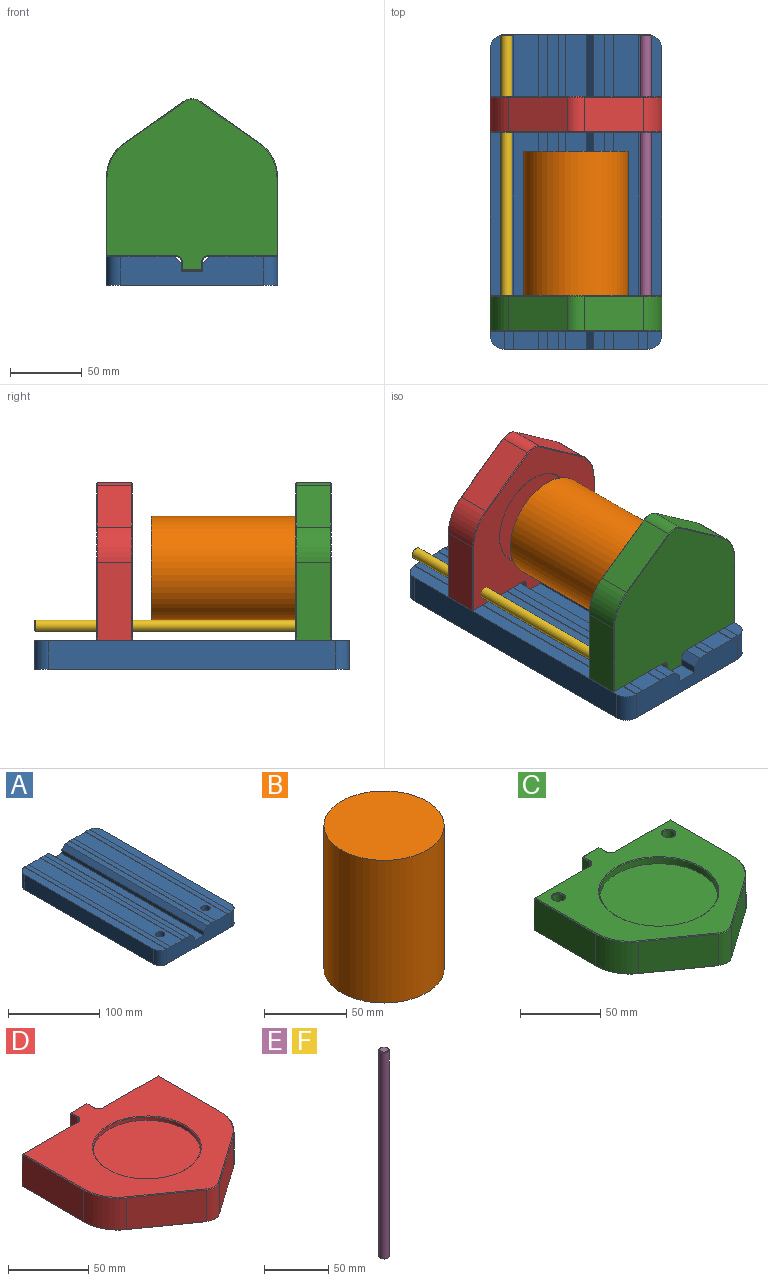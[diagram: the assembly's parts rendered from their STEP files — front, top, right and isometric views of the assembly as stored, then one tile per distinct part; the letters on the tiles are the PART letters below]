
ASSEMBLY  parts=6 mates=10
PART A: 34 faces, bbox 120x220x20.5 mm
  f0: plane 220x18mm, normal (0,0,1), area 3878.3mm2, adj f7,f11,f21,f29,f31
  f1: plane 220x7.45mm, normal (0,0,1), area 1639mm2, adj f7,f11,f18,f28
  f2: plane 220x10mm, normal (0,0,1), area 2157.1mm2, adj f6,f12,f13,f25
  f3: plane 220x18mm, normal (0,0,1), area 3878.3mm2, adj f7,f11,f20,f22,f26
  f4: plane 220x120mm, normal (0,0,-1), area 26150.7mm2, adj f6,f7,f8,f9,f10,f11,f12,f13
  f5: plane 220x10mm, normal (0,0,1), area 2157.1mm2, adj f8,f9,f10,f32
  f6: cylinder r=10mm len=20mm, axis (0,0,-1), area 314.2mm2, adj f2,f4,f7,f13
  f7: plane 100x20.5mm, normal (0,-1,0), area 1833mm2, adj f0,f1,f3,f4,f6,f8,f14,f15
  f8: cylinder r=10mm len=20mm, axis (0,0,-1), area 314.2mm2, adj f4,f5,f7,f9
  f9: plane 200x20mm, normal (1,0,0), area 4000mm2, adj f4,f5,f8,f10
  f10: cylinder r=10mm len=20mm, axis (0,0,-1), area 314.2mm2, adj f4,f5,f9,f11
  f11: plane 100x20.5mm, normal (0,1,0), area 1833mm2, adj f0,f1,f3,f4,f10,f12,f14,f15
  f12: cylinder r=10mm len=20mm, axis (0,0,-1), area 314.2mm2, adj f2,f4,f11,f13
  f13: plane 200x20mm, normal (-1,0,0), area 4000mm2, adj f2,f4,f6,f12
  f14: plane 220x7.45mm, normal (0,0,1), area 1639mm2, adj f7,f11,f19,f23
  f15: plane 220x5.2mm, normal (1,0,0), area 1144mm2, adj f7,f11,f17,f19
  f16: plane 220x5.2mm, normal (-1,0,0), area 1144mm2, adj f7,f11,f17,f18
  f17: plane 220x15.1mm, normal (0,0,1), area 3322mm2, adj f7,f11,f15,f16
  f18: plane 220x5mm, normal (-0.71,0,0.71), area 1555.6mm2, adj f1,f7,f11,f16
  f19: plane 220x5mm, normal (0.71,0,0.71), area 1555.6mm2, adj f7,f11,f14,f15
  f20: cylinder r=5.1mm len=20mm, axis (0,0,1), area 640.9mm2, adj f3,f4
  f21: cylinder r=5.1mm len=20mm, axis (0,0,1), area 640.9mm2, adj f0,f4
  f22: plane 220x0.5mm, normal (-1,0,0), area 110mm2, adj f3,f7,f11,f24
  f23: plane 220x0.5mm, normal (1,0,0), area 110mm2, adj f7,f11,f14,f24
  f24: plane 220x6mm, normal (0,0,1), area 1320mm2, adj f7,f11,f22,f23
  f25: plane 220x0.5mm, normal (-1,0,0), area 110mm2, adj f2,f7,f11,f27
  f26: plane 220x0.5mm, normal (1,0,0), area 110mm2, adj f3,f7,f11,f27
  f27: plane 220x6mm, normal (0,0,1), area 1320mm2, adj f7,f11,f25,f26
  f28: plane 220x0.5mm, normal (-1,0,0), area 110mm2, adj f1,f7,f11,f30
  f29: plane 220x0.5mm, normal (1,0,0), area 110mm2, adj f0,f7,f11,f30
  f30: plane 220x6mm, normal (0,0,1), area 1320mm2, adj f7,f11,f28,f29
  f31: plane 220x0.5mm, normal (-1,0,0), area 110mm2, adj f0,f7,f11,f33
  f32: plane 220x0.5mm, normal (1,0,0), area 110mm2, adj f5,f7,f11,f33
  f33: plane 220x6mm, normal (0,0,1), area 1320mm2, adj f7,f11,f31,f32
PART B: 3 faces, bbox 73x73x106 mm
  f0: cylinder r=36.5mm len=106mm, axis (0,0,-1), area 24309.6mm2, adj f1,f2
  f1: plane 73x73mm, normal (0,0,1), area 4185.4mm2, adj f0
  f2: plane 73x73mm, normal (0,0,-1), area 4185.4mm2, adj f0
PART C: 65 faces, bbox 120x120.2x25 mm
  f0: plane 119.2x119mm, normal (0,0,1), area 6258.4mm2, adj f26,f27,f28,f29,f30,f31,f32,f33
  f1: plane 24x13.9mm, normal (0,1,0), area 333.6mm2, adj f41,f42,f48,f49
  f2: plane 24x5.7mm, normal (-1,0,0), area 136.8mm2, adj f3,f43,f49,f53
  f3: cylinder r=4mm len=24mm, axis (0,0,1), area 150.8mm2, adj f2,f4,f38,f55
  f4: plane 48.55x24mm, normal (0,1,0), area 1070.2mm2, adj f3,f5,f36,f57,f60
  f5: plane 54.43x24mm, normal (-1,0,0), area 1306.3mm2, adj f4,f14,f34,f59
  f6: plane 41.51x29.22mm, normal (-0.58,-0.82,0), area 1218.3mm2, adj f7,f14,f30,f56
  f7: cylinder r=10mm len=24mm, axis (0,0,1), area 294.4mm2, adj f6,f8,f28,f54
  f8: plane 41.51x29.22mm, normal (0.58,-0.82,0), area 1218.3mm2, adj f7,f15,f26,f52
  f9: plane 54.43x24mm, normal (1,0,0), area 1306.3mm2, adj f10,f15,f29,f47
  f10: plane 48.55x24mm, normal (0,1,0), area 1070.2mm2, adj f9,f11,f31,f44,f61
  f11: cylinder r=4mm len=24mm, axis (0,0,1), area 150.8mm2, adj f10,f12,f33,f39
  f12: plane 24x5.7mm, normal (1,0,0), area 136.8mm2, adj f11,f35,f40,f41
  f13: plane 119.2x119mm, normal (0,0,-1), area 10803.5mm2, adj f39,f40,f44,f47,f48,f50,f52,f53
  f14: cylinder r=30mm len=24.53mm, axis (0,0,1), area 689.4mm2, adj f5,f6,f32,f58
  f15: cylinder r=30mm len=24.53mm, axis (0,0,1), area 689.4mm2, adj f8,f9,f27,f50
  f16: cylinder r=37mm len=74mm, axis (0,0,1), area 1046.2mm2, adj f17,f63
  f17: plane 74x74mm, normal (0,0,1), area 4300.8mm2, adj f16
  f18: cylinder r=4mm len=14.5mm, axis (0,0,1), area 364.4mm2, adj f19,f64
  f19: plane 8x8mm, normal (0,0,1), area 50.3mm2, adj f18
  f20: cylinder r=4mm len=14.5mm, axis (0,0,1), area 364.4mm2, adj f21,f62
  f21: plane 8x8mm, normal (0,0,1), area 50.3mm2, adj f20
  f22: cylinder r=5mm len=14.5mm, axis (0,1,0), area 455.5mm2, adj f23,f61
  f23: plane 10x10mm, normal (0,1,0), area 78.5mm2, adj f22
  f24: cylinder r=5mm len=14.5mm, axis (0,1,0), area 455.5mm2, adj f25,f60
  f25: plane 10x10mm, normal (0,1,0), area 78.5mm2, adj f24
  f26: plane 41.8x29.62mm, normal (0.41,-0.58,0.71), area 35.9mm2, adj f0,f8,f27,f28
  f27: cone r=29.5mm half-angle=45deg, axis (0,0,-1), area 20.1mm2, adj f0,f15,f26,f29
  f28: cone r=9.5mm half-angle=45deg, axis (0,0,-1), area 8.5mm2, adj f0,f7,f26,f30
  f29: plane 54.43x0.5mm, normal (0.71,0,0.71), area 38.3mm2, adj f0,f9,f27,f31
  f30: plane 41.8x29.62mm, normal (-0.41,-0.58,0.71), area 35.9mm2, adj f0,f6,f28,f32
  f31: plane 48.55x0.5mm, normal (0,0.71,0.71), area 34.2mm2, adj f0,f10,f29,f33
  f32: cone r=29.5mm half-angle=45deg, axis (0,0,-1), area 20.1mm2, adj f0,f14,f30,f34
  f33: cone r=4mm half-angle=45deg, axis (0,0,1), area 4.7mm2, adj f0,f11,f31,f35
  f34: plane 54.43x0.5mm, normal (-0.71,0,0.71), area 38.3mm2, adj f0,f5,f32,f36
  f35: plane 5.7x0.5mm, normal (0.71,0,0.71), area 4mm2, adj f0,f12,f33,f37
  f36: plane 48.55x0.5mm, normal (0,0.71,0.71), area 34.2mm2, adj f0,f4,f34,f38
  f37: plane 0.5x0.5mm, normal (0.58,0.58,0.58), area 0.2mm2, adj f35,f41,f42
  f38: cone r=4mm half-angle=45deg, axis (0,0,1), area 4.7mm2, adj f0,f3,f36,f43
  f39: cone r=4.5mm half-angle=45deg, axis (0,0,-1), area 4.7mm2, adj f11,f13,f40,f44
  f40: plane 5.7x0.5mm, normal (0.71,0,-0.71), area 4mm2, adj f12,f13,f39,f45
  f41: plane 24x0.5mm, normal (0.71,0.71,0), area 17mm2, adj f1,f12,f37,f45
  f42: plane 13.9x0.5mm, normal (0,0.71,0.71), area 9.8mm2, adj f0,f1,f37,f46
  f43: plane 5.7x0.5mm, normal (-0.71,0,0.71), area 4mm2, adj f0,f2,f38,f46
  f44: plane 48.55x0.5mm, normal (0,0.71,-0.71), area 34.2mm2, adj f10,f13,f39,f47
  f45: plane 0.5x0.5mm, normal (0.58,0.58,-0.58), area 0.2mm2, adj f40,f41,f48
  f46: plane 0.5x0.5mm, normal (-0.58,0.58,0.58), area 0.2mm2, adj f42,f43,f49
  f47: plane 54.43x0.5mm, normal (0.71,0,-0.71), area 38.3mm2, adj f9,f13,f44,f50
  f48: plane 13.9x0.5mm, normal (0,0.71,-0.71), area 9.8mm2, adj f1,f13,f45,f51
  f49: plane 24x0.5mm, normal (-0.71,0.71,0), area 17mm2, adj f1,f2,f46,f51
  f50: cone r=29.5mm half-angle=45deg, axis (0,0,1), area 20.1mm2, adj f13,f15,f47,f52
  f51: plane 0.5x0.5mm, normal (-0.58,0.58,-0.58), area 0.2mm2, adj f48,f49,f53
  f52: plane 41.8x29.62mm, normal (0.41,-0.58,-0.71), area 35.9mm2, adj f8,f13,f50,f54
  f53: plane 5.7x0.5mm, normal (-0.71,0,-0.71), area 4mm2, adj f2,f13,f51,f55
  f54: cone r=10mm half-angle=45deg, axis (0,0,1), area 8.5mm2, adj f7,f13,f52,f56
  f55: cone r=4.5mm half-angle=45deg, axis (0,0,-1), area 4.7mm2, adj f3,f13,f53,f57
  f56: plane 41.8x29.62mm, normal (-0.41,-0.58,-0.71), area 35.9mm2, adj f6,f13,f54,f58
  f57: plane 48.55x0.5mm, normal (0,0.71,-0.71), area 34.2mm2, adj f4,f13,f55,f59
  f58: cone r=29.5mm half-angle=45deg, axis (0,0,1), area 20.1mm2, adj f13,f14,f56,f59
  f59: plane 54.43x0.5mm, normal (-0.71,0,-0.71), area 38.3mm2, adj f5,f13,f57,f58
  f60: cone r=5.5mm half-angle=45deg, axis (0,1,0), area 23.3mm2, adj f4,f24
  f61: cone r=5mm half-angle=45deg, axis (0,1,0), area 23.3mm2, adj f10,f22
  f62: cone r=4.5mm half-angle=45deg, axis (0,0,1), area 18.9mm2, adj f0,f20
  f63: cone r=37mm half-angle=45deg, axis (0,0,1), area 165.5mm2, adj f0,f16
  f64: cone r=4mm half-angle=45deg, axis (0,0,1), area 18.9mm2, adj f0,f18
PART D: 47 faces, bbox 120x120.2x25 mm
  f0: plane 24x14.9mm, normal (0,1,0), area 357.6mm2, adj f1,f11,f23,f37
  f1: plane 24x6.2mm, normal (-1,0,0), area 148.8mm2, adj f0,f2,f21,f39
  f2: cylinder r=4mm len=24mm, axis (0,0,1), area 150.8mm2, adj f1,f3,f19,f41
  f3: plane 48.55x24mm, normal (0,1,0), area 1165.2mm2, adj f2,f4,f18,f43
  f4: plane 54.43x24mm, normal (-1,0,0), area 1306.3mm2, adj f3,f14,f20,f45
  f5: plane 41.51x29.22mm, normal (-0.58,-0.82,0), area 1218.3mm2, adj f6,f14,f24,f42
  f6: cylinder r=10mm len=24mm, axis (0,0,1), area 294.4mm2, adj f5,f7,f26,f40
  f7: plane 41.51x29.22mm, normal (0.58,-0.82,0), area 1218.3mm2, adj f6,f15,f28,f38
  f8: plane 54.43x24mm, normal (1,0,0), area 1306.3mm2, adj f9,f15,f31,f34
  f9: plane 48.55x24mm, normal (0,1,0), area 1165.2mm2, adj f8,f10,f29,f32
  f10: cylinder r=4mm len=24mm, axis (0,0,1), area 150.8mm2, adj f9,f11,f27,f33
  f11: plane 24x6.2mm, normal (1,0,0), area 148.8mm2, adj f0,f10,f25,f35
  f12: plane 119.2x119mm, normal (0,0,-1), area 10803.5mm2, adj f32,f33,f34,f35,f36,f37,f38,f39
  f13: plane 119.2x119mm, normal (0,0,1), area 7183.5mm2, adj f18,f19,f20,f21,f22,f23,f24,f25
  f14: cylinder r=30mm len=24.53mm, axis (0,0,1), area 689.4mm2, adj f4,f5,f22,f44
  f15: cylinder r=30mm len=24.53mm, axis (0,0,1), area 689.4mm2, adj f7,f8,f30,f36
  f16: cylinder r=33.45mm len=66.89mm, axis (0,0,1), area 525.4mm2, adj f17,f46
  f17: plane 66.89x66.89mm, normal (0,0,1), area 3514.1mm2, adj f16
  f18: plane 48.55x0.5mm, normal (0,0.71,0.71), area 34.2mm2, adj f3,f13,f19,f20
  f19: cone r=4mm half-angle=45deg, axis (0,0,1), area 4.7mm2, adj f2,f13,f18,f21
  f20: plane 54.43x0.5mm, normal (-0.71,0,0.71), area 38.3mm2, adj f4,f13,f18,f22
  f21: plane 6.2x0.5mm, normal (-0.71,0,0.71), area 4.2mm2, adj f1,f13,f19,f23
  f22: cone r=29.5mm half-angle=45deg, axis (0,0,-1), area 20.1mm2, adj f13,f14,f20,f24
  f23: plane 14.9x0.5mm, normal (0,0.71,0.71), area 10.2mm2, adj f0,f13,f21,f25
  f24: plane 41.8x29.62mm, normal (-0.41,-0.58,0.71), area 35.9mm2, adj f5,f13,f22,f26
  f25: plane 6.2x0.5mm, normal (0.71,0,0.71), area 4.2mm2, adj f11,f13,f23,f27
  f26: cone r=9.5mm half-angle=45deg, axis (0,0,-1), area 8.5mm2, adj f6,f13,f24,f28
  f27: cone r=4mm half-angle=45deg, axis (0,0,1), area 4.7mm2, adj f10,f13,f25,f29
  f28: plane 41.8x29.62mm, normal (0.41,-0.58,0.71), area 35.9mm2, adj f7,f13,f26,f30
  f29: plane 48.55x0.5mm, normal (0,0.71,0.71), area 34.2mm2, adj f9,f13,f27,f31
  f30: cone r=29.5mm half-angle=45deg, axis (0,0,-1), area 20.1mm2, adj f13,f15,f28,f31
  f31: plane 54.43x0.5mm, normal (0.71,0,0.71), area 38.3mm2, adj f8,f13,f29,f30
  f32: plane 48.55x0.5mm, normal (0,0.71,-0.71), area 34.2mm2, adj f9,f12,f33,f34
  f33: cone r=4.5mm half-angle=45deg, axis (0,0,-1), area 4.7mm2, adj f10,f12,f32,f35
  f34: plane 54.43x0.5mm, normal (0.71,0,-0.71), area 38.3mm2, adj f8,f12,f32,f36
  f35: plane 6.2x0.5mm, normal (0.71,0,-0.71), area 4.2mm2, adj f11,f12,f33,f37
  f36: cone r=29.5mm half-angle=45deg, axis (0,0,1), area 20.1mm2, adj f12,f15,f34,f38
  f37: plane 14.9x0.5mm, normal (0,0.71,-0.71), area 10.2mm2, adj f0,f12,f35,f39
  f38: plane 41.8x29.62mm, normal (0.41,-0.58,-0.71), area 35.9mm2, adj f7,f12,f36,f40
  f39: plane 6.2x0.5mm, normal (-0.71,0,-0.71), area 4.2mm2, adj f1,f12,f37,f41
  f40: cone r=10mm half-angle=45deg, axis (0,0,1), area 8.5mm2, adj f6,f12,f38,f42
  f41: cone r=4.5mm half-angle=45deg, axis (0,0,-1), area 4.7mm2, adj f2,f12,f39,f43
  f42: plane 41.8x29.62mm, normal (-0.41,-0.58,-0.71), area 35.9mm2, adj f5,f12,f40,f44
  f43: plane 48.55x0.5mm, normal (0,0.71,-0.71), area 34.2mm2, adj f3,f12,f41,f45
  f44: cone r=29.5mm half-angle=45deg, axis (0,0,1), area 20.1mm2, adj f12,f14,f42,f45
  f45: plane 54.43x0.5mm, normal (-0.71,0,-0.71), area 38.3mm2, adj f4,f12,f43,f44
  f46: cone r=33.45mm half-angle=45deg, axis (0,0,1), area 149.7mm2, adj f13,f16
PART E: 5 faces, bbox 8x8x197.5 mm
  f0: cylinder r=3.98mm len=196.5mm, axis (0,0,-1), area 4907.7mm2, adj f3,f4
  f1: plane 6.95x6.95mm, normal (0,0,1), area 37.9mm2, adj f3
  f2: plane 6.95x6.95mm, normal (0,0,-1), area 37.9mm2, adj f4
  f3: cone r=3.47mm half-angle=45deg, axis (0,0,-1), area 16.5mm2, adj f0,f1
  f4: cone r=3.98mm half-angle=45deg, axis (0,0,1), area 16.5mm2, adj f0,f2
PART F: same geometry as E
PLACE A t=(-0.09,-99.98,-5.89)mm fixed
PLACE B rot(axis=(0,-0.71,0.71),180deg) t=(-0.09,28.52,64.61)mm
PLACE C rot(axis=(-1,0,0),90deg) t=(-0.09,-72.48,64.61)mm
PLACE D rot(axis=(0,-0.71,0.71),180deg) t=(-0.09,41.67,39.35)mm
PLACE E rot(axis=(-1,0,0),90deg) t=(48.41,-87.48,24.61)mm
PLACE F rot(axis=(0,0.71,0.71),180deg) t=(-48.59,-87.48,24.61)mm
MATE fastened B.f0 <-> C.f16  axis (0,-1,0) through (-0.09,-77.48,64.61)mm
MATE cylindrical D.f16 <-> B.f0  axis (0,-1,0) through (-0.09,44.67,64.61)mm
MATE cylindrical A.f21 <-> C.f22  axis (0,0,-1) through (34.91,-84.98,-5.89)mm
MATE fastened E.f0 <-> C.f20  axis (0,-1,0) through (48.41,-87.48,24.61)mm
MATE cylindrical E.f0 <-> C.f20  axis (0,-1,0) through (48.41,11.27,24.61)mm
MATE planar A.f30 <-> D.f9  axis (0,0,1) through (22.91,110.02,14.61)mm
MATE cylindrical C.f18 <-> F.f0  axis (0,1,0) through (-48.59,-72.48,24.61)mm
MATE fastened F.f0 <-> C.f18  axis (0,-1,0) through (-48.59,-87.48,24.61)mm
MATE planar A.f33 <-> C.f22  axis (0,0,1) through (46.91,0.02,14.61)mm
MATE cylindrical A.f20 <-> C.f24  axis (0,0,-1) through (-35.09,-84.98,-5.89)mm
